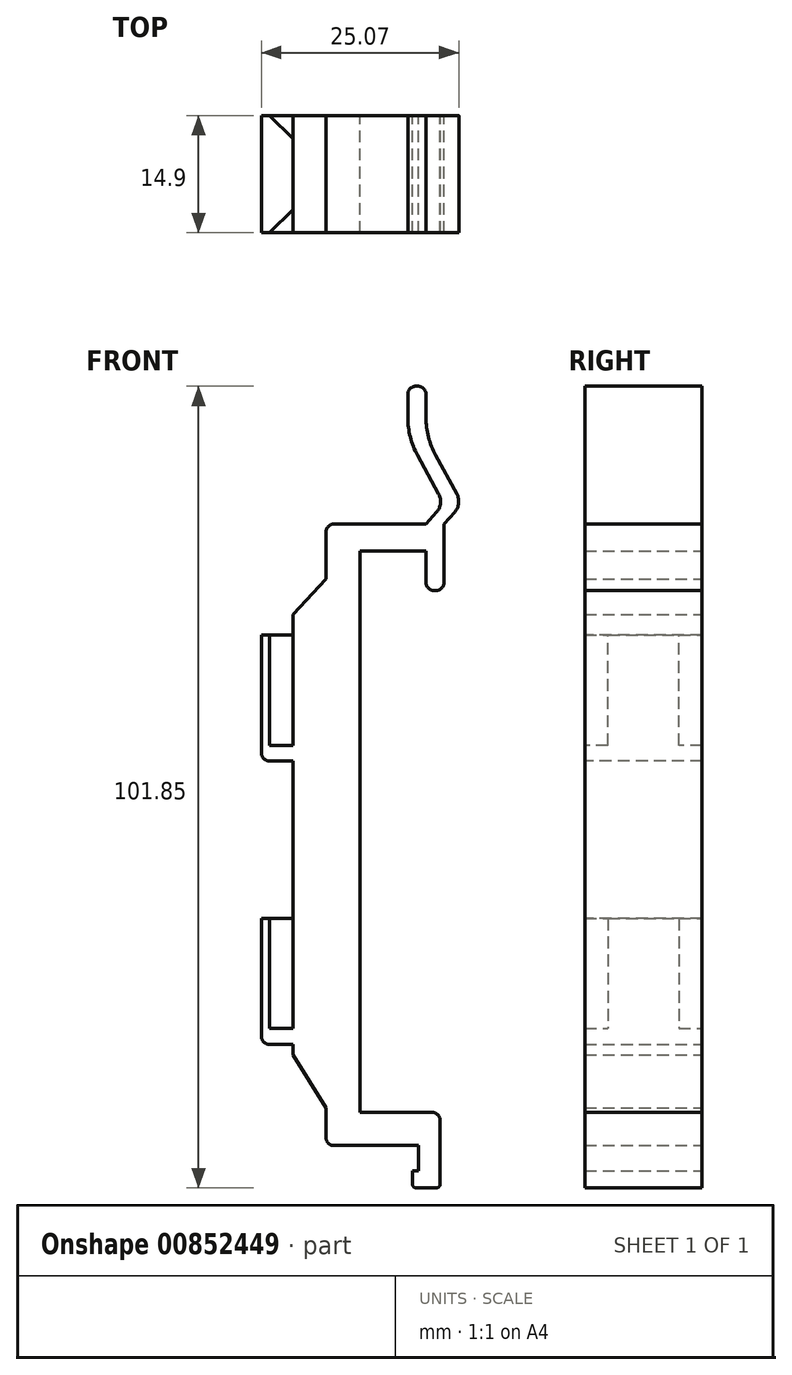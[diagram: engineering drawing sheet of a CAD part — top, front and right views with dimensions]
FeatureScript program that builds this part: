
annotation { "Feature Type Name" : "Feature", "Feature Type Description" : "" }
export const myFeature = defineFeature(function(context is Context, id is Id, definition is map)
    precondition{}
    {
        {
            var Q0;
            Q0=qCreatedBy(makeId("Front.planeOp"),FACE);
            var sketch = newSketch(context, id + "F0", { "sketchPlane" : qUnion([Q0])});
            skLineSegment(sketch, "E0", {"start": v(-4.3, -35.05) * mm, "end": v(-8.5, -28.33) * mm});
            skLineSegment(sketch, "E1", {"start": v(-8.5, -28.33) * mm, "end": v(-8.5, 27.6) * mm});
            skLineSegment(sketch, "E2", {"start": v(-8.5, 27.6) * mm, "end": v(-4.3, 32.1) * mm});
            skLineSegment(sketch, "E3", {"start": v(-4.3, 32.1) * mm, "end": v(-4.3, 38.1) * mm});
            skLineSegment(sketch, "E4", {"start": v(-3.3, 39.1) * mm, "end": v(8.4, 39.1) * mm});
            skLineSegment(sketch, "E5", {"start": v(10.7, 39.1) * mm, "end": v(10.7, 31.65) * mm});
            skLineSegment(sketch, "E6", {"start": v(9.7, 30.65) * mm, "end": v(9.4, 30.65) * mm});
            skLineSegment(sketch, "E7", {"start": v(8.4, 31.65) * mm, "end": v(8.4, 35.65) * mm});
            skLineSegment(sketch, "E8", {"start": v(8.4, 35.65) * mm, "end": v(0, 35.65) * mm});
            skLineSegment(sketch, "E9", {"start": v(0, 35.65) * mm, "end": v(0, -35.65) * mm});
            skLineSegment(sketch, "E10", {"start": v(0, -35.65) * mm, "end": v(9.2, -35.65) * mm});
            skLineSegment(sketch, "E11", {"start": v(10.2, -36.65) * mm, "end": v(10.2, -44.75) * mm});
            skLineSegment(sketch, "E12", {"start": v(9.7, -45.25) * mm, "end": v(7.2, -45.25) * mm});
            skLineSegment(sketch, "E13", {"start": v(6.7, -44.75) * mm, "end": v(6.7, -43.05) * mm});
            skLineSegment(sketch, "E14", {"start": v(6.7, -43.05) * mm, "end": v(7.45, -43.05) * mm});
            skLineSegment(sketch, "E15", {"start": v(7.45, -43.05) * mm, "end": v(7.45, -39.85) * mm});
            skLineSegment(sketch, "E16", {"start": v(7.45, -39.85) * mm, "end": v(-3.3, -39.85) * mm});
            skLineSegment(sketch, "E17", {"start": v(-4.3, -38.85) * mm, "end": v(-4.3, -35.05) * mm});
            skLineSegment(sketch, "E18", {"start": v(8.4, 55.6) * mm, "end": v(8.4, 52.64) * mm});
            skLineSegment(sketch, "E19", {"start": v(9.63, 47.84) * mm, "end": v(12.32, 42.91) * mm});
            skLineSegment(sketch, "E20", {"start": v(12.06, 40.62) * mm, "end": v(10.7, 39.1) * mm});
            skLineSegment(sketch, "E21", {"start": v(7.4, 56.6) * mm, "end": v(7.1, 56.6) * mm});
            skLineSegment(sketch, "E22", {"start": v(6.1, 55.6) * mm, "end": v(6.1, 52.64) * mm});
            skLineSegment(sketch, "E23", {"start": v(7.33, 47.84) * mm, "end": v(10.02, 42.91) * mm});
            skLineSegment(sketch, "E24", {"start": v(9.76, 40.62) * mm, "end": v(8.4, 39.1) * mm});
            skPoint(sketch, "E25.visualSharp", {"position": v(6.1, 50.08) * mm});
            skArc(sketch, "E25.filletArc", {"start": v(6.1, 52.64) * mm, "mid": v(6.41, 50.16) * mm, "end": v(7.33, 47.84) * mm});
            skPoint(sketch, "E26.visualSharp", {"position": v(8.4, 50.08) * mm});
            skArc(sketch, "E26.filletArc", {"start": v(8.4, 52.64) * mm, "mid": v(8.71, 50.16) * mm, "end": v(9.63, 47.84) * mm});
            skPoint(sketch, "E27.visualSharp", {"position": v(10.7, 41.67) * mm});
            skArc(sketch, "E27.filletArc", {"start": v(9.76, 40.62) * mm, "mid": v(10.25, 41.72) * mm, "end": v(10.02, 42.91) * mm});
            skPoint(sketch, "E28.visualSharp", {"position": v(13, 41.67) * mm});
            skArc(sketch, "E28.filletArc", {"start": v(12.06, 40.62) * mm, "mid": v(12.55, 41.72) * mm, "end": v(12.32, 42.91) * mm});
            skPoint(sketch, "E29.visualSharp", {"position": v(8.4, 56.6) * mm});
            skArc(sketch, "E29.filletArc", {"start": v(8.4, 55.6) * mm, "mid": v(8.1, 56.3) * mm, "end": v(7.4, 56.6) * mm});
            skPoint(sketch, "E30.visualSharp", {"position": v(6.1, 56.6) * mm});
            skArc(sketch, "E30.filletArc", {"start": v(7.1, 56.6) * mm, "mid": v(6.4, 56.3) * mm, "end": v(6.1, 55.6) * mm});
            skPoint(sketch, "E31.visualSharp", {"position": v(10.7, 30.65) * mm});
            skArc(sketch, "E31.filletArc", {"start": v(9.7, 30.65) * mm, "mid": v(10.4, 30.94) * mm, "end": v(10.7, 31.65) * mm});
            skPoint(sketch, "E32.visualSharp", {"position": v(8.4, 30.65) * mm});
            skArc(sketch, "E32.filletArc", {"start": v(8.4, 31.65) * mm, "mid": v(8.7, 30.94) * mm, "end": v(9.4, 30.65) * mm});
            skPoint(sketch, "E33.visualSharp", {"position": v(-4.3, 39.1) * mm});
            skArc(sketch, "E33.filletArc", {"start": v(-3.3, 39.1) * mm, "mid": v(-4, 38.8) * mm, "end": v(-4.3, 38.1) * mm});
            skPoint(sketch, "E34.visualSharp", {"position": v(-4.3, -39.85) * mm});
            skArc(sketch, "E34.filletArc", {"start": v(-4.3, -38.85) * mm, "mid": v(-4, -39.56) * mm, "end": v(-3.3, -39.85) * mm});
            skPoint(sketch, "E35.visualSharp", {"position": v(10.2, -35.65) * mm});
            skArc(sketch, "E35.filletArc", {"start": v(10.2, -36.65) * mm, "mid": v(9.9, -35.94) * mm, "end": v(9.2, -35.65) * mm});
            skPoint(sketch, "E36.visualSharp", {"position": v(10.2, -45.25) * mm});
            skArc(sketch, "E36.filletArc", {"start": v(9.7, -45.25) * mm, "mid": v(10.05, -45.1) * mm, "end": v(10.2, -44.75) * mm});
            skPoint(sketch, "E37.visualSharp", {"position": v(6.7, -45.25) * mm});
            skArc(sketch, "E37.filletArc", {"start": v(6.7, -44.75) * mm, "mid": v(6.85, -45.1) * mm, "end": v(7.2, -45.25) * mm});
            skSolve(sketch);
        }
        {
            var Q0;
            Q0=qSketchRegion(id+"F0",true);
            extrude(context, id + "F1", {"entities" : qUnion([Q0]), "offsetDistance" : 25 * mm, "depth" : 14.9 * mm, "symmetric" : true});
        }
        {
            var Q0;
            Q0=qCreatedBy(makeId("Top.planeOp"),FACE);
            cPlane(context, id + "F2", {"entities" : qUnion([Q0]), "cplaneType" : CPlaneType.OFFSET, "offset" : 25 * mm, "width" : 150 * mm, "height" : 150 * mm});
        }
        {
            var Q0;
            Q0=qCreatedBy(makeId("Top.planeOp"),FACE);
            cPlane(context, id + "F3", {"entities" : qUnion([Q0]), "cplaneType" : CPlaneType.OFFSET, "offset" : 25 * mm, "oppositeDirection" : true, "width" : 150 * mm, "height" : 150 * mm});
        }
        {
            var Q0;
            Q0=qCreatedBy(makeId("Top.planeOp"),FACE);
            var sketch = newSketch(context, id + "F4", { "sketchPlane" : qUnion([Q0])});
            skLineSegment(sketch, "E38", {"start": v(-14.36, 0) * mm, "end": v(0, 0) * mm, "construction": true});
            skLineSegment(sketch, "E39.MirrorCS", {"start": v(-12.5, 7.45) * mm, "end": v(-12.5, -7.45) * mm});
            skPoint(sketch, "E40.visualSharp", {"position": v(-12.5, -7.45) * mm});
            skPoint(sketch, "E41.visualSharp", {"position": v(-12.5, 7.45) * mm});
            skPoint(sketch, "E42.orphan", {"position": v(-12.5, 0) * mm});
            skLineSegment(sketch, "E43", {"start": v(-12.5, 7.45) * mm, "end": v(-11.45, 7.45) * mm});
            skLineSegment(sketch, "E44", {"start": v(-11.45, 7.45) * mm, "end": v(-8.5, 4.5) * mm});
            skLineSegment(sketch, "E45", {"start": v(-8.5, 0) * mm, "end": v(-8.5, 4.5) * mm});
            skLineSegment(sketch, "E46.MirrorCS", {"start": v(-11.45, -7.45) * mm, "end": v(-8.5, -4.5) * mm});
            skLineSegment(sketch, "E47.MirrorCS", {"start": v(-8.5, 0) * mm, "end": v(-8.5, -4.5) * mm});
            skLineSegment(sketch, "E48.MirrorCS", {"start": v(-12.5, -7.45) * mm, "end": v(-11.45, -7.45) * mm});
            skSolve(sketch);
        }
        {
            var Q0;
            Q0=qCreatedBy(id+"F3.planeOp",FACE);
            var sketch = newSketch(context, id + "F5", { "sketchPlane" : qUnion([Q0])});
            skLineSegment(sketch, "E49.0.0", {"start": v(-12.5, -7.45) * mm, "end": v(-11.45, -7.45) * mm});
            skLineSegment(sketch, "E49.0.1", {"start": v(-11.45, -7.45) * mm, "end": v(-8.5, -4.5) * mm});
            skLineSegment(sketch, "E49.0.2", {"start": v(-8.5, -4.5) * mm, "end": v(-8.5, 0) * mm});
            skLineSegment(sketch, "E49.0.3", {"start": v(-8.5, 0) * mm, "end": v(-8.5, 4.5) * mm});
            skLineSegment(sketch, "E49.0.4", {"start": v(-8.5, 4.5) * mm, "end": v(-11.45, 7.45) * mm});
            skLineSegment(sketch, "E49.0.5", {"start": v(-11.45, 7.45) * mm, "end": v(-12.5, 7.45) * mm});
            skLineSegment(sketch, "E49.0.6", {"start": v(-12.5, 7.45) * mm, "end": v(-12.5, -7.45) * mm});
            skSolve(sketch);
        }
        {
            var Q0;
            Q0=qCreatedBy(id+"F2.planeOp",FACE);
            var sketch = newSketch(context, id + "F6", { "sketchPlane" : qUnion([Q0])});
            skLineSegment(sketch, "E50.0.0", {"start": v(-12.5, -7.45) * mm, "end": v(-11.45, -7.45) * mm});
            skLineSegment(sketch, "E50.0.1", {"start": v(-11.45, -7.45) * mm, "end": v(-8.5, -4.5) * mm});
            skLineSegment(sketch, "E50.0.2", {"start": v(-8.5, -4.5) * mm, "end": v(-8.5, 0) * mm});
            skLineSegment(sketch, "E50.0.3", {"start": v(-8.5, 0) * mm, "end": v(-8.5, 4.5) * mm});
            skLineSegment(sketch, "E50.0.4", {"start": v(-8.5, 4.5) * mm, "end": v(-11.45, 7.45) * mm});
            skLineSegment(sketch, "E50.0.5", {"start": v(-11.45, 7.45) * mm, "end": v(-12.5, 7.45) * mm});
            skLineSegment(sketch, "E50.0.6", {"start": v(-12.5, 7.45) * mm, "end": v(-12.5, -7.45) * mm});
            skSolve(sketch);
        }
        {
            var Q0;
            Q0=makeQuery(id+"F6.imprint","IMPRINT",FACE,{"disambiguationData":[TD([[makeQuery(id+"F6.imprint","IMPRINT",EDGE,{"derivedFrom":sQuery(id+"F6.wireOp",EDGE,"E50.0.0")}),1.0]])]});
            extrude(context, id + "F7", {"entities" : qUnion([Q0]), "operationType" : NewBodyOperationType.ADD, "oppositeDirection" : true, "depth" : 14 * mm, "offsetDistance" : 25 * mm});
        }
        {
            var Q0;
            Q0=makeQuery(id+"F5.imprint","IMPRINT",FACE,{"disambiguationData":[TD([[makeQuery(id+"F5.imprint","IMPRINT",EDGE,{"derivedFrom":sQuery(id+"F5.wireOp",EDGE,"E49.0.0")}),1.0]])]});
            extrude(context, id + "F8", {"entities" : qUnion([Q0]), "operationType" : NewBodyOperationType.ADD, "depth" : 14 * mm, "offsetDistance" : 25 * mm});
        }
        {
            var Q0;
            Q0=makeQuery(id+"F8.opExtrude","CAP_FACE",FACE,{"disambiguationData":[OSD([sQuery(id+"F5.wireOp",EDGE,"E49.0.0"),sQuery(id+"F5.wireOp",EDGE,"E49.0.1"),sQuery(id+"F5.wireOp",EDGE,"E49.0.2"),sQuery(id+"F5.wireOp",EDGE,"E49.0.3"),sQuery(id+"F5.wireOp",EDGE,"E49.0.4"),sQuery(id+"F5.wireOp",EDGE,"E49.0.5"),sQuery(id+"F5.wireOp",EDGE,"E49.0.6")])],"isStart":true});
            var sketch = newSketch(context, id + "F9", { "sketchPlane" : qUnion([Q0])});
            skLineSegment(sketch, "E51.bottom", {"start": v(-12.5, -7.45) * mm, "end": v(-8.5, -7.45) * mm});
            skLineSegment(sketch, "E51.top", {"start": v(-12.5, 7.45) * mm, "end": v(-8.5, 7.45) * mm});
            skLineSegment(sketch, "E51.left", {"start": v(-12.5, -7.45) * mm, "end": v(-12.5, 7.45) * mm});
            skLineSegment(sketch, "E51.right", {"start": v(-8.5, -7.45) * mm, "end": v(-8.5, 7.45) * mm});
            skSolve(sketch);
        }
        {
            var Q0;
            Q0=makeQuery(id+"F7.opExtrude","CAP_FACE",FACE,{"disambiguationData":[OSD([sQuery(id+"F6.wireOp",EDGE,"E50.0.0"),sQuery(id+"F6.wireOp",EDGE,"E50.0.1"),sQuery(id+"F6.wireOp",EDGE,"E50.0.2"),sQuery(id+"F6.wireOp",EDGE,"E50.0.3"),sQuery(id+"F6.wireOp",EDGE,"E50.0.4"),sQuery(id+"F6.wireOp",EDGE,"E50.0.5"),sQuery(id+"F6.wireOp",EDGE,"E50.0.6")])],"isStart":false});
            var sketch = newSketch(context, id + "F10", { "sketchPlane" : qUnion([Q0])});
            skLineSegment(sketch, "E52.bottom", {"start": v(-12.5, -7.45) * mm, "end": v(-8.5, -7.45) * mm});
            skLineSegment(sketch, "E52.top", {"start": v(-12.5, 7.45) * mm, "end": v(-8.5, 7.45) * mm});
            skLineSegment(sketch, "E52.left", {"start": v(-12.5, -7.45) * mm, "end": v(-12.5, 7.45) * mm});
            skLineSegment(sketch, "E52.right", {"start": v(-8.5, -7.45) * mm, "end": v(-8.5, 7.45) * mm});
            skSolve(sketch);
        }
        {
            var Q0;
            {var subQ1=makeQuery(id+"F7.opExtrude","CAP_EDGE",EDGE,{"disambiguationData":[OSD([sQuery(id+"F6.wireOp",EDGE,"E50.0.1")])],"isStart":false});Q0=makeQuery(id+"F10.imprint","IMPRINT",FACE,{"disambiguationData":[TD([[makeQuery(id+"F10.imprint","IMPRINT",EDGE,{"derivedFrom":subQ1}),1.0]])]});}
            var Q1;
            {var subQ0=sQuery(id+"F10.wireOp",EDGE,"E52.left");Q1=makeQuery(id+"F10.imprint","IMPRINT",FACE,{"disambiguationData":[TD([[makeQuery(id+"F10.imprint","IMPRINT",EDGE,{"derivedFrom":subQ0}),-1.0]])]});}
            var Q2;
            {var subQ1=makeQuery(id+"F7.opExtrude","CAP_EDGE",EDGE,{"disambiguationData":[OSD([sQuery(id+"F6.wireOp",EDGE,"E50.0.4")])],"isStart":false});Q2=makeQuery(id+"F10.imprint","IMPRINT",FACE,{"disambiguationData":[TD([[makeQuery(id+"F10.imprint","IMPRINT",EDGE,{"derivedFrom":subQ1}),1.0]])]});}
            extrude(context, id + "F11", {"entities" : qUnion([Q0, Q1, Q2]), "operationType" : NewBodyOperationType.ADD, "depth" : 2 * mm, "offsetDistance" : 25 * mm});
        }
        {
            var Q0;
            {var subQ0=sQuery(id+"F9.wireOp",EDGE,"E51.left");Q0=makeQuery(id+"F9.imprint","IMPRINT",FACE,{"disambiguationData":[TD([[makeQuery(id+"F9.imprint","IMPRINT",EDGE,{"derivedFrom":subQ0}),-1.0]])]});}
            var Q1;
            {var subQ1=makeQuery(id+"F8.opExtrude","CAP_EDGE",EDGE,{"disambiguationData":[OSD([sQuery(id+"F5.wireOp",EDGE,"E49.0.4")])],"isStart":true});Q1=makeQuery(id+"F9.imprint","IMPRINT",FACE,{"disambiguationData":[TD([[makeQuery(id+"F9.imprint","IMPRINT",EDGE,{"derivedFrom":subQ1}),1.0]])]});}
            var Q2;
            {var subQ1=makeQuery(id+"F8.opExtrude","CAP_EDGE",EDGE,{"disambiguationData":[OSD([sQuery(id+"F5.wireOp",EDGE,"E49.0.1")])],"isStart":true});Q2=makeQuery(id+"F9.imprint","IMPRINT",FACE,{"disambiguationData":[TD([[makeQuery(id+"F9.imprint","IMPRINT",EDGE,{"derivedFrom":subQ1}),1.0]])]});}
            extrude(context, id + "F12", {"entities" : qUnion([Q0, Q1, Q2]), "operationType" : NewBodyOperationType.ADD, "depth" : 2 * mm, "offsetDistance" : 25 * mm});
        }
        {
            var Q0;
            Q0=makeQuery(id+"F12.opExtrude","CAP_EDGE",EDGE,{"disambiguationData":[OSD([sQuery(id+"F9.wireOp",EDGE,"E51.left")])],"isStart":false});
            var Q1;
            Q1=makeQuery(id+"F11.opExtrude","CAP_EDGE",EDGE,{"disambiguationData":[OSD([sQuery(id+"F10.wireOp",EDGE,"E52.left")])],"isStart":false});
            var Q2;
            Q2=makeQuery(id+"F11.opExtrude","CAP_EDGE",EDGE,{"disambiguationData":[OSD([sQuery(id+"F10.wireOp",EDGE,"E52.right")])],"isStart":false});
            var Q3;
            Q3=makeQuery(id+"F12.opExtrude","CAP_EDGE",EDGE,{"disambiguationData":[OSD([sQuery(id+"F9.wireOp",EDGE,"E51.right")])],"isStart":false});
            fillet(context, id + "F13", {"entities" : qUnion([Q0, Q1, Q2, Q3]), "radius" : 1 * mm, "tangentPropagation" : true, "allowEdgeOverflow" : false});
        }
    });
